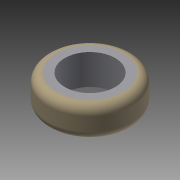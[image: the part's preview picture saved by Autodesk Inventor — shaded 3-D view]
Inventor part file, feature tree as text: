
AUTODESK INVENTOR PART (.ipt)
format: ipt  version: 2015 (Build 190159000, 159)  size: 119,808 bytes
history: native  units: mm
features: extrude x1, fillet x1, sketch x1
ambient origin geometry x8: Origin, YZ Plane, XZ Plane, XY Plane, X Axis, Y Axis, Z Axis, Center Point
bodies: 实体1 (feature_tree)
feature tree (3):
  extrude  "拉伸1"  Depth=5.0mm
  fillet  "圆角1"  Radius=18.0mm
  sketch  "草图1"  dims[d0=30.0mm d1=50.0mm d2=18.0mm d3=0.0mm d4=5.0mm]
